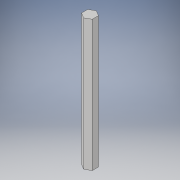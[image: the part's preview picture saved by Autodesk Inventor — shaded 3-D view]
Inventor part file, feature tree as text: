
AUTODESK INVENTOR PART (.ipt)
format: ipt  version: 2018 (Build 220112000, 112)  size: 95,232 bytes
history: native  units: in
note: dims shown in document units (in); Inventor stores cm internally (conversion verified against a paired STEP export)
features: extrude x1, sketch x1
ambient origin geometry x8: Origin, YZ Plane, XZ Plane, XY Plane, X Axis, Y Axis, Z Axis, Center Point
bodies: Solid1 (feature_tree)
feature tree (2):
  extrude  "Extrusion1"  Depth=4.565in TaperAngle=0.0deg
  sketch  "Sketch1"  dims[d0=0.375in d1=4.565in d2=0.0in]
